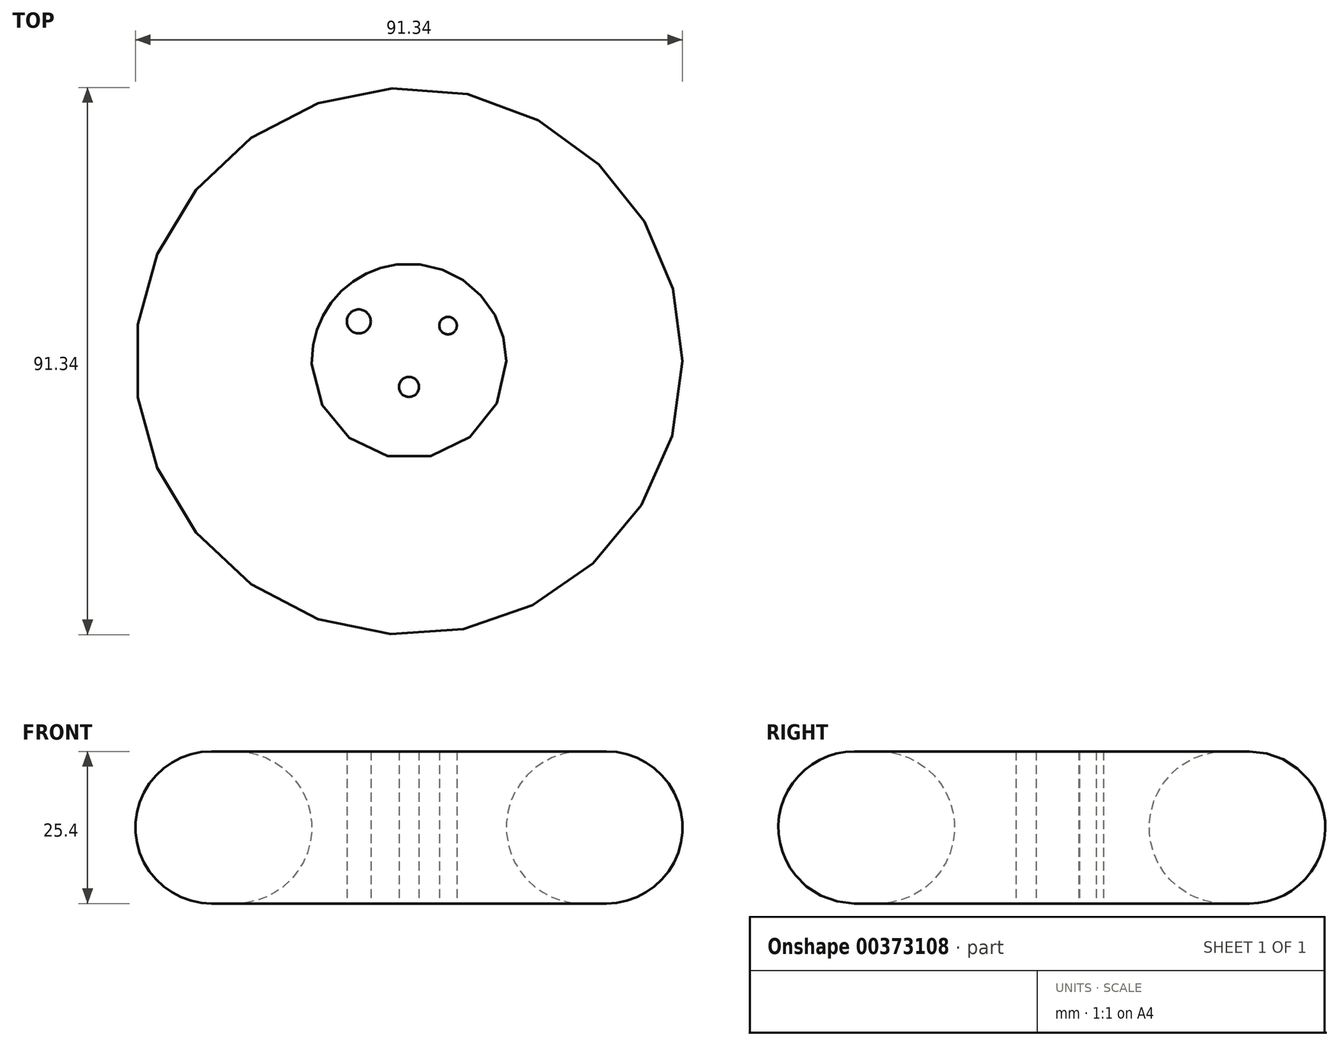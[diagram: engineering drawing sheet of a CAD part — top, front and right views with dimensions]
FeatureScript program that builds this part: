
annotation { "Feature Type Name" : "Feature", "Feature Type Description" : "" }
export const myFeature = defineFeature(function(context is Context, id is Id, definition is map)
    precondition{}
    {
        {
            var Q0;
            Q0=qCreatedBy(makeId("Top.planeOp"),FACE);
            var sketch = newSketch(context, id + "F0", { "sketchPlane" : qUnion([Q0])});
            skCircle(sketch, "E0", {"center": v(0, 0) * mm, "radius": 45.67 * mm});
            skCircle(sketch, "E1", {"center": v(0, 0) * mm, "radius": 16.26 * mm});
            skLineSegment(sketch, "E2", {"start": v(-30.8, 13.5) * mm, "end": v(-24.2, 13.5) * mm});
            skLineSegment(sketch, "E3", {"start": v(6.37, 28.68) * mm, "end": v(0, 22.56) * mm});
            skLineSegment(sketch, "E4", {"start": v(-24.2, 22.56) * mm, "end": v(-15.7, 20.5) * mm});
            skLineSegment(sketch, "E5", {"start": v(-24.2, 4.13) * mm, "end": v(-33.56, -3.85) * mm});
            skLineSegment(sketch, "E6", {"start": v(-12.05, 29.83) * mm, "end": v(-12.05, 22.56) * mm});
            skLineSegment(sketch, "E7", {"start": v(-15.7, 13.5) * mm, "end": v(-16.7, 9.38) * mm});
            skLineSegment(sketch, "E8", {"start": v(-44.7, 9.38) * mm, "end": v(-37.33, 0) * mm});
            skLineSegment(sketch, "E9", {"start": v(-30.8, -11.5) * mm, "end": v(-37.33, -19.3) * mm});
            skLineSegment(sketch, "E10", {"start": v(-3.72, 36.78) * mm, "end": v(-5.3, 32.49) * mm});
            skLineSegment(sketch, "E11", {"start": v(-24.2, 26.2) * mm, "end": v(-19.95, 31.28) * mm});
            skPoint(sketch, "E11.startSnap0", {"position": v(-12.05, 26.2) * mm});
            skPoint(sketch, "E11.endSnap0", {"position": v(-19.95, 21.53) * mm});
            skLineSegment(sketch, "E12", {"start": v(3.23, 36.43) * mm, "end": v(6.37, 33.8) * mm});
            skLineSegment(sketch, "E13", {"start": v(-19.95, -11.5) * mm, "end": v(-16.7, -19.3) * mm});
            skLineSegment(sketch, "E14", {"start": v(-33.56, -19.3) * mm, "end": v(-33.56, -30.97) * mm});
            skLineSegment(sketch, "E15", {"start": v(-5.3, -19.3) * mm, "end": v(-6.83, -25.63) * mm});
            skLineSegment(sketch, "E16", {"start": v(-15.7, -30.97) * mm, "end": v(-19.95, -27.42) * mm});
            skLineSegment(sketch, "E17", {"start": v(-8.6, -34.78) * mm, "end": v(-5.3, -37.53) * mm});
            skLineSegment(sketch, "E18", {"start": v(6.37, 20.5) * mm, "end": v(10.03, 17.44) * mm});
            skLineSegment(sketch, "E19", {"start": v(20.58, 17.44) * mm, "end": v(25.9, 22.56) * mm});
            skLineSegment(sketch, "E20", {"start": v(14.07, 20.5) * mm, "end": v(16.05, 28.68) * mm});
            skLineSegment(sketch, "E21", {"start": v(20.58, 4.13) * mm, "end": v(25.9, 2.85) * mm});
            skLineSegment(sketch, "E22", {"start": v(35.72, 9.38) * mm, "end": v(25.9, 11.36) * mm});
            skLineSegment(sketch, "E23", {"start": v(0, -30.97) * mm, "end": v(10.03, -30.97) * mm});
            skLineSegment(sketch, "E24", {"start": v(6.37, -25.63) * mm, "end": v(7.64, -19.3) * mm});
            skLineSegment(sketch, "E25", {"start": v(20.58, -11.5) * mm, "end": v(21.84, -15.54) * mm});
            skLineSegment(sketch, "E26", {"start": v(21.84, -25.63) * mm, "end": v(20.76, -30.97) * mm});
            skLineSegment(sketch, "E27", {"start": v(16.05, -25.63) * mm, "end": v(16.05, -19.3) * mm});
            skLineSegment(sketch, "E28", {"start": v(30.38, -3.85) * mm, "end": v(28.84, -11.5) * mm});
            skLineSegment(sketch, "E29", {"start": v(25.9, -19.3) * mm, "end": v(32.41, -20.04) * mm});
            skLineSegment(sketch, "E30", {"start": v(37.26, 4.13) * mm, "end": v(36.56, 0) * mm});
            skCircle(sketch, "E31", {"center": v(-8.38, 6.63) * mm, "radius": 2 * mm});
            skCircle(sketch, "E32", {"center": v(0, -4.3) * mm, "radius": 1.68 * mm});
            skCircle(sketch, "E33", {"center": v(6.52, 5.94) * mm, "radius": 1.46 * mm});
            skSolve(sketch);
        }
        {
            var Q0;
            Q0=makeQuery(id+"F0.imprint","IMPRINT",FACE,{"disambiguationData":[TD([[makeQuery(id+"F0.imprint","IMPRINT",EDGE,{"derivedFrom":sQuery(id+"F0.wireOp",EDGE,"E1")}),-1.0]])]});
            var Q1;
            Q1=makeQuery(id+"F0.imprint","IMPRINT",FACE,{"disambiguationData":[TD([[makeQuery(id+"F0.imprint","IMPRINT",EDGE,{"derivedFrom":sQuery(id+"F0.wireOp",EDGE,"E32")}),1.0]])]});
            var Q2;
            Q2=makeQuery(id+"F0.imprint","IMPRINT",FACE,{"disambiguationData":[TD([[makeQuery(id+"F0.imprint","IMPRINT",EDGE,{"derivedFrom":sQuery(id+"F0.wireOp",EDGE,"E31")}),1.0]])]});
            var Q3;
            Q3=makeQuery(id+"F0.imprint","IMPRINT",FACE,{"disambiguationData":[TD([[makeQuery(id+"F0.imprint","IMPRINT",EDGE,{"derivedFrom":sQuery(id+"F0.wireOp",EDGE,"E33")}),1.0]])]});
            extrude(context, id + "F1", {"entities" : qUnion([Q0, Q1, Q2, Q3]), "depth" : 25.4 * mm});
        }
        {
            var Q0;
            Q0=makeQuery(id+"F1.opExtrude","SWEPT_FACE",FACE,{"disambiguationData":[OSD([sQuery(id+"F0.wireOp",EDGE,"E0")])]});
            var Q1;
            Q1=makeQuery(id+"F1.opExtrude","CAP_EDGE",EDGE,{"disambiguationData":[OSD([sQuery(id+"F0.wireOp",EDGE,"E0")])],"isStart":false});
            var Q2;
            Q2=makeQuery(id+"F1.opExtrude","SWEPT_FACE",FACE,{"disambiguationData":[OSD([sQuery(id+"F0.wireOp",EDGE,"E1")])]});
            var Q3;
            Q3=makeQuery(id+"F1.opExtrude","CAP_EDGE",EDGE,{"disambiguationData":[OSD([sQuery(id+"F0.wireOp",EDGE,"E1")])],"isStart":true});
            fillet(context, id + "F2", {"entities" : qUnion([Q0, Q1, Q2, Q3]), "radius" : 12.7 * mm, "tangentPropagation" : true, "allowEdgeOverflow" : false});
        }
    });
